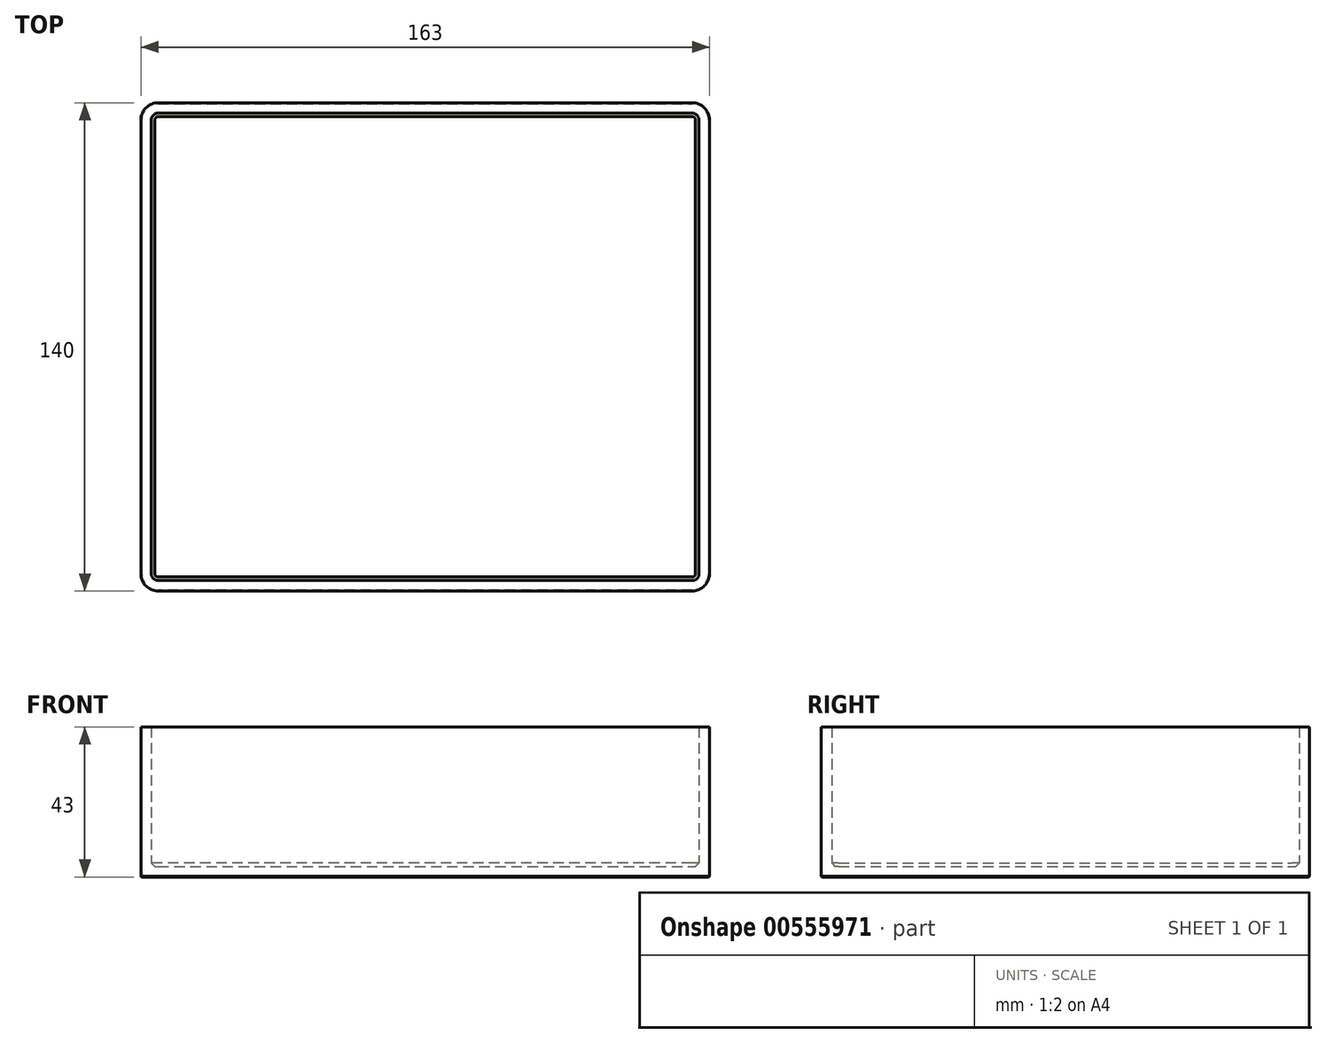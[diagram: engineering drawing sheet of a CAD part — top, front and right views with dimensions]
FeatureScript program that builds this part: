
annotation { "Feature Type Name" : "Feature", "Feature Type Description" : "" }
export const myFeature = defineFeature(function(context is Context, id is Id, definition is map)
    precondition{}
    {
        {
            var Q0;
            Q0=qCreatedBy(makeId("Top.planeOp"),FACE);
            var sketch = newSketch(context, id + "F0", { "sketchPlane" : qUnion([Q0])});
            skLineSegment(sketch, "E0.bottom", {"start": v(57.5, 46) * mm, "end": v(-57.5, 46) * mm});
            skLineSegment(sketch, "E0.top", {"start": v(57.5, -46) * mm, "end": v(-57.5, -46) * mm});
            skLineSegment(sketch, "E0.left", {"start": v(57.5, 46) * mm, "end": v(57.5, -46) * mm});
            skLineSegment(sketch, "E0.right", {"start": v(-57.5, 46) * mm, "end": v(-57.5, -46) * mm});
            skPoint(sketch, "E0.middle", {"position": v(0, 0) * mm});
            skLineSegment(sketch, "E1.bottom", {"start": v(61.5, -50) * mm, "end": v(-61.5, -50) * mm});
            skLineSegment(sketch, "E1.top", {"start": v(61.5, 50) * mm, "end": v(-61.5, 50) * mm});
            skLineSegment(sketch, "E1.left", {"start": v(61.5, -50) * mm, "end": v(61.5, 50) * mm});
            skLineSegment(sketch, "E1.right", {"start": v(-61.5, -50) * mm, "end": v(-61.5, 50) * mm});
            skLineSegment(sketch, "E2.bottom", {"start": v(81.5, -70) * mm, "end": v(-81.5, -70) * mm});
            skLineSegment(sketch, "E2.top", {"start": v(81.5, 70) * mm, "end": v(-81.5, 70) * mm});
            skLineSegment(sketch, "E2.left", {"start": v(81.5, -70) * mm, "end": v(81.5, 70) * mm});
            skLineSegment(sketch, "E2.right", {"start": v(-81.5, -70) * mm, "end": v(-81.5, 70) * mm});
            skSolve(sketch);
        }
        {
            var Q0;
            Q0=makeQuery(id+"F0.imprint","IMPRINT",FACE,{"disambiguationData":[TD([[makeQuery(id+"F0.imprint","IMPRINT",EDGE,{"derivedFrom":sQuery(id+"F0.wireOp",EDGE,"E1.bottom")}),1.0]])]});
            var Q1;
            Q1=makeQuery(id+"F0.imprint","IMPRINT",FACE,{"disambiguationData":[TD([[makeQuery(id+"F0.imprint","IMPRINT",EDGE,{"derivedFrom":sQuery(id+"F0.wireOp",EDGE,"E0.bottom")}),1.0]])]});
            var Q2;
            Q2=makeQuery(id+"F0.imprint","IMPRINT",FACE,{"disambiguationData":[TD([[makeQuery(id+"F0.imprint","IMPRINT",EDGE,{"derivedFrom":sQuery(id+"F0.wireOp",EDGE,"E0.bottom")}),-1.0]])]});
            extrude(context, id + "F1", {"entities" : qUnion([Q0, Q1, Q2]), "depth" : 3 * mm, "offsetDistance" : 25 * mm});
        }
        {
            var Q0;
            Q0=makeQuery(id+"F1.opExtrude","CAP_FACE",FACE,{"disambiguationData":[OSD([sQuery(id+"F0.wireOp",EDGE,"E2.bottom"),sQuery(id+"F0.wireOp",EDGE,"E2.top"),sQuery(id+"F0.wireOp",EDGE,"E2.left"),sQuery(id+"F0.wireOp",EDGE,"E2.right")])],"isStart":false});
            var sketch = newSketch(context, id + "F2", { "sketchPlane" : qUnion([Q0])});
            skLineSegment(sketch, "E3.0", {"start": v(81.5, -70) * mm, "end": v(-81.5, -70) * mm});
            skLineSegment(sketch, "E4.0", {"start": v(-81.5, -70) * mm, "end": v(-81.5, 70) * mm});
            skLineSegment(sketch, "E5.0", {"start": v(81.5, 70) * mm, "end": v(-81.5, 70) * mm});
            skLineSegment(sketch, "E6.0", {"start": v(81.5, -70) * mm, "end": v(81.5, 70) * mm});
            skLineSegment(sketch, "E7.0", {"start": v(-78.5, -67) * mm, "end": v(-78.5, 67) * mm});
            skLineSegment(sketch, "E7.1", {"start": v(78.5, -67) * mm, "end": v(-78.5, -67) * mm});
            skLineSegment(sketch, "E7.2", {"start": v(78.5, -67) * mm, "end": v(78.5, 67) * mm});
            skLineSegment(sketch, "E7.3", {"start": v(78.5, 67) * mm, "end": v(-78.5, 67) * mm});
            skSolve(sketch);
        }
        {
            var Q0;
            Q0=makeQuery(id+"F2.imprint","IMPRINT",FACE,{"disambiguationData":[TD([[makeQuery(id+"F2.imprint","IMPRINT",EDGE,{"derivedFrom":sQuery(id+"F2.wireOp",EDGE,"E3.0")}),-1.0]])]});
            var Q1;
            Q1=sQuery(id+"F2.wireOp",EDGE,"E7.0");
            extrude(context, id + "F3", {"entities" : qUnion([Q0]), "operationType" : NewBodyOperationType.ADD, "surfaceEntities" : qUnion([Q1]), "depth" : 40 * mm, "offsetDistance" : 25 * mm});
        }
        {
            var Q0;
            Q0=makeQuery(id+"F3.boolean.opBoolean","MERGE",EDGE,{"derivedFrom":[makeQuery(id+"F1.opExtrude","SWEPT_EDGE",EDGE,{"disambiguationData":[OSD([sQuery(id+"F0.wireOp",EDGE,"E2.bottom"),sQuery(id+"F0.wireOp",EDGE,"E2.right")])]}),makeQuery(id+"F3.opExtrude","SWEPT_EDGE",EDGE,{"disambiguationData":[OSD([sQuery(id+"F2.wireOp",EDGE,"E3.0"),sQuery(id+"F2.wireOp",EDGE,"E4.0")])]})]});
            var Q1;
            Q1=makeQuery(id+"F3.boolean.opBoolean","MERGE",EDGE,{"derivedFrom":[makeQuery(id+"F1.opExtrude","SWEPT_EDGE",EDGE,{"disambiguationData":[OSD([sQuery(id+"F0.wireOp",EDGE,"E2.bottom"),sQuery(id+"F0.wireOp",EDGE,"E2.left")])]}),makeQuery(id+"F3.opExtrude","SWEPT_EDGE",EDGE,{"disambiguationData":[OSD([sQuery(id+"F2.wireOp",EDGE,"E3.0"),sQuery(id+"F2.wireOp",EDGE,"E6.0")])]})]});
            var Q2;
            Q2=makeQuery(id+"F3.boolean.opBoolean","MERGE",EDGE,{"derivedFrom":[makeQuery(id+"F1.opExtrude","SWEPT_EDGE",EDGE,{"disambiguationData":[OSD([sQuery(id+"F0.wireOp",EDGE,"E2.top"),sQuery(id+"F0.wireOp",EDGE,"E2.left")])]}),makeQuery(id+"F3.opExtrude","SWEPT_EDGE",EDGE,{"disambiguationData":[OSD([sQuery(id+"F2.wireOp",EDGE,"E5.0"),sQuery(id+"F2.wireOp",EDGE,"E6.0")])]})]});
            var Q3;
            Q3=makeQuery(id+"F3.boolean.opBoolean","MERGE",EDGE,{"derivedFrom":[makeQuery(id+"F1.opExtrude","SWEPT_EDGE",EDGE,{"disambiguationData":[OSD([sQuery(id+"F0.wireOp",EDGE,"E2.top"),sQuery(id+"F0.wireOp",EDGE,"E2.right")])]}),makeQuery(id+"F3.opExtrude","SWEPT_EDGE",EDGE,{"disambiguationData":[OSD([sQuery(id+"F2.wireOp",EDGE,"E4.0"),sQuery(id+"F2.wireOp",EDGE,"E5.0")])]})]});
            fillet(context, id + "F4", {"entities" : qUnion([Q0, Q1, Q2, Q3]), "radius" : 5 * mm, "tangentPropagation" : true, "allowEdgeOverflow" : false});
        }
        {
            var Q0;
            Q0=makeQuery(id+"F3.opExtrude","SWEPT_EDGE",EDGE,{"disambiguationData":[OSD([sQuery(id+"F2.wireOp",EDGE,"E7.1"),sQuery(id+"F2.wireOp",EDGE,"E7.2")])]});
            var Q1;
            Q1=makeQuery(id+"F3.opExtrude","SWEPT_EDGE",EDGE,{"disambiguationData":[OSD([sQuery(id+"F2.wireOp",EDGE,"E7.0"),sQuery(id+"F2.wireOp",EDGE,"E7.1")])]});
            var Q2;
            Q2=makeQuery(id+"F3.opExtrude","SWEPT_EDGE",EDGE,{"disambiguationData":[OSD([sQuery(id+"F2.wireOp",EDGE,"E7.2"),sQuery(id+"F2.wireOp",EDGE,"E7.3")])]});
            var Q3;
            Q3=makeQuery(id+"F3.opExtrude","SWEPT_EDGE",EDGE,{"disambiguationData":[OSD([sQuery(id+"F2.wireOp",EDGE,"E7.0"),sQuery(id+"F2.wireOp",EDGE,"E7.3")])]});
            fillet(context, id + "F5", {"entities" : qUnion([Q0, Q1, Q2, Q3]), "radius" : 2 * mm, "tangentPropagation" : true, "allowEdgeOverflow" : false});
        }
        {
            var Q0;
            Q0=makeQuery(id+"F1.opExtrude","CAP_FACE",FACE,{"disambiguationData":[OSD([sQuery(id+"F0.wireOp",EDGE,"E2.bottom"),sQuery(id+"F0.wireOp",EDGE,"E2.top"),sQuery(id+"F0.wireOp",EDGE,"E2.left"),sQuery(id+"F0.wireOp",EDGE,"E2.right")])],"isStart":true});
            chamfer(context, id + "F6", {"entities" : qUnion([Q0]), "width" : 0.25 * mm, "tangentPropagation" : true});
        }
        {
            var Q0;
            Q0=makeQuery(id+"F1.opExtrude","CAP_FACE",FACE,{"disambiguationData":[OSD([sQuery(id+"F0.wireOp",EDGE,"E2.bottom"),sQuery(id+"F0.wireOp",EDGE,"E2.top"),sQuery(id+"F0.wireOp",EDGE,"E2.left"),sQuery(id+"F0.wireOp",EDGE,"E2.right")])],"isStart":false});
            chamfer(context, id + "F7", {"entities" : qUnion([Q0]), "width" : 1 * mm, "tangentPropagation" : true});
        }
    });
